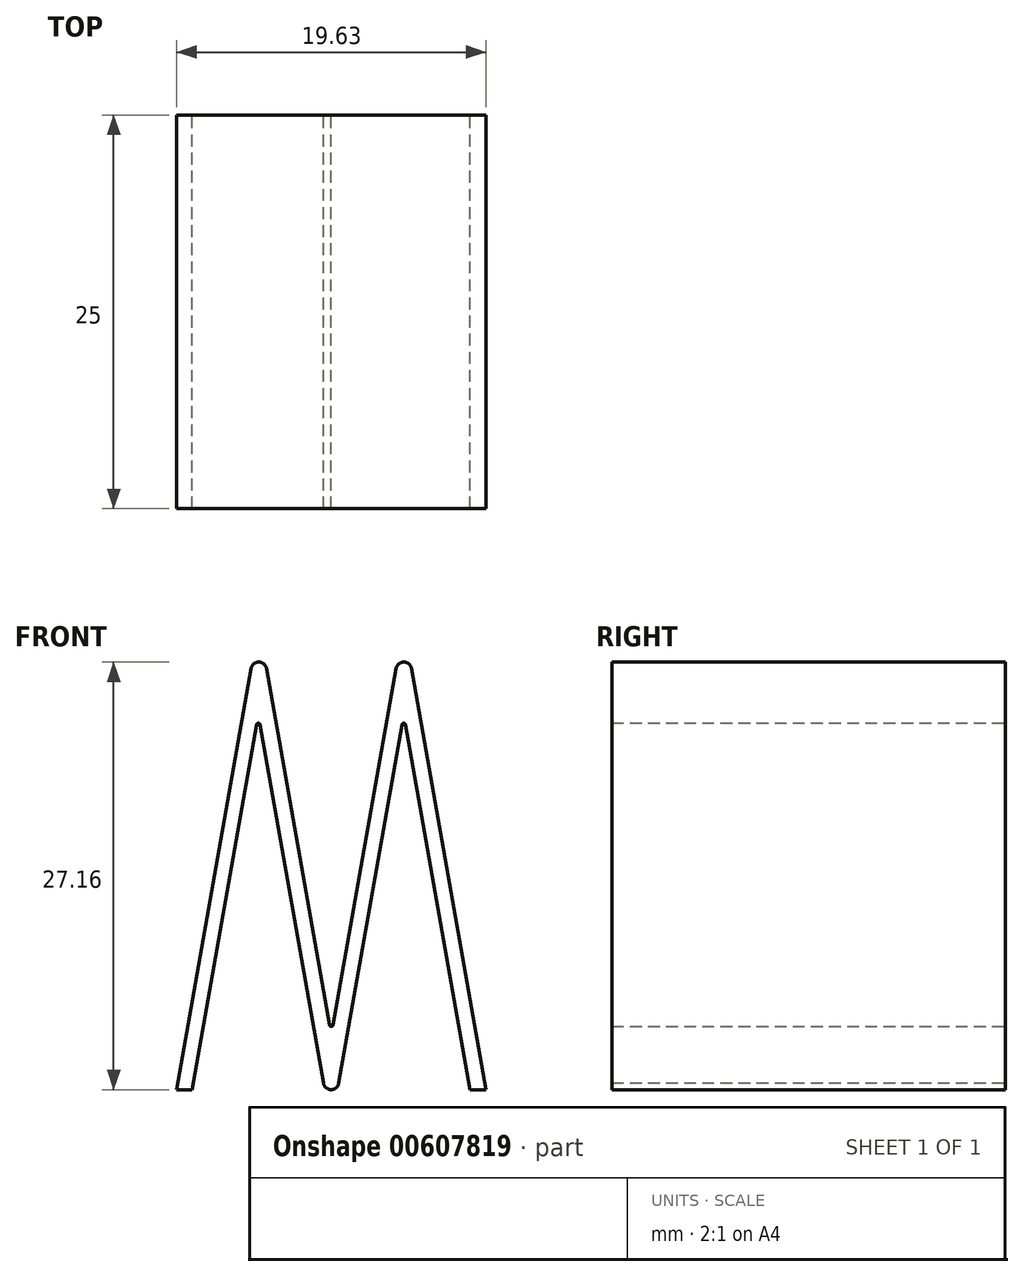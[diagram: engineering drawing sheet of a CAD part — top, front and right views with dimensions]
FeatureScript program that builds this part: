
annotation { "Feature Type Name" : "Feature", "Feature Type Description" : "" }
export const myFeature = defineFeature(function(context is Context, id is Id, definition is map)
    precondition{}
    {
        {
            var Q0;
            Q0=qCreatedBy(makeId("Front.planeOp"),FACE);
            var sketch = newSketch(context, id + "F0", { "sketchPlane" : qUnion([Q0])});
            skLineSegment(sketch, "E0", {"start": v(-0.5, 26.75) * mm, "end": v(-4.48, 4.12) * mm});
            skLineSegment(sketch, "E1", {"start": v(-4.63, 0) * mm, "end": v(-4.61, 0) * mm});
            skLineSegment(sketch, "E2", {"start": v(-4.14, 0.41) * mm, "end": v(-0.12, 23.17) * mm});
            skLineSegment(sketch, "E3.MirrorCS", {"start": v(0.5, 26.75) * mm, "end": v(5.2, 0) * mm});
            skLineSegment(sketch, "E4.MirrorCS", {"start": v(4.2, 0) * mm, "end": v(0.12, 23.17) * mm});
            skLineSegment(sketch, "E5.MirrorCS", {"start": v(5.2, 0) * mm, "end": v(4.2, 0) * mm});
            skPoint(sketch, "E6.visualSharp", {"position": v(0, 23.87) * mm});
            skArc(sketch, "E6.filletArc", {"start": v(0.12, 23.17) * mm, "mid": v(0, 23.28) * mm, "end": v(-0.12, 23.17) * mm});
            skPoint(sketch, "E7.visualSharp", {"position": v(0, 29.54) * mm});
            skArc(sketch, "E7.filletArc", {"start": v(0.5, 26.75) * mm, "mid": v(0, 27.16) * mm, "end": v(-0.5, 26.75) * mm});
            skPoint(sketch, "E8.visualSharp", {"position": v(-5.2, 0) * mm});
            skArc(sketch, "E8.filletArc", {"start": v(-5.1, 0.43) * mm, "mid": v(-4.94, 0.12) * mm, "end": v(-4.61, 0) * mm});
            skPoint(sketch, "E9.visualSharp", {"position": v(-4.2, 0) * mm});
            skArc(sketch, "E9.filletArc", {"start": v(-4.63, 0) * mm, "mid": v(-4.3, 0.12) * mm, "end": v(-4.14, 0.41) * mm});
            skLineSegment(sketch, "E10", {"start": v(-5.1, 0.59) * mm, "end": v(-4.1, 0.59) * mm, "construction": true});
            skLineSegment(sketch, "E11", {"start": v(-4.14, 0.41) * mm, "end": v(-5.1, 0.41) * mm, "construction": true});
            skCircle(sketch, "E12", {"center": v(-5.1, 0.41) * mm, "radius": 1.01 * mm, "construction": true});
            skCircle(sketch, "E13", {"center": v(-4.1, 0.59) * mm, "radius": 1.01 * mm, "construction": true});
            skLineSegment(sketch, "E14", {"start": v(-5.1, 0.41) * mm, "end": v(-4.1, 0.59) * mm, "construction": true});
            skLineSegment(sketch, "E15", {"start": v(-4.46, -0.37) * mm, "end": v(-4.76, 1.37) * mm, "construction": true});
            skLineSegment(sketch, "E16", {"start": v(-4.62, 0.59) * mm, "end": v(-4.62, 0.9) * mm, "construction": true});
            skLineSegment(sketch, "E17.MirrorCS", {"start": v(-5.1, 0.41) * mm, "end": v(-9.12, 23.17) * mm});
            skLineSegment(sketch, "E18.MirrorCS", {"start": v(-13.45, 0) * mm, "end": v(-9.37, 23.17) * mm});
            skArc(sketch, "E19.MirrorCS", {"start": v(-9.37, 23.17) * mm, "mid": v(-9.24, 23.28) * mm, "end": v(-9.12, 23.17) * mm});
            skLineSegment(sketch, "E20.MirrorCS", {"start": v(-14.42, 0) * mm, "end": v(-13.45, 0) * mm});
            skLineSegment(sketch, "E21", {"start": v(-4.6, 0.5) * mm, "end": v(-4.6, 0.64) * mm, "construction": true});
            skLineSegment(sketch, "E22.MirrorCS", {"start": v(-8.72, 26.75) * mm, "end": v(-4.73, 4.12) * mm});
            skLineSegment(sketch, "E23.MirrorCS", {"start": v(-9.7, 26.75) * mm, "end": v(-14.42, 0) * mm});
            skArc(sketch, "E24.MirrorCS", {"start": v(-9.7, 26.75) * mm, "mid": v(-9.21, 27.16) * mm, "end": v(-8.72, 26.75) * mm});
            skLineSegment(sketch, "E25.trimOffspring", {"start": v(-4.1, 0.59) * mm, "end": v(-4.1, 0.59) * mm});
            skPoint(sketch, "E26.visualSharp", {"position": v(-4.6, 3.42) * mm});
            skArc(sketch, "E26.filletArc", {"start": v(-4.73, 4.12) * mm, "mid": v(-4.6, 4.02) * mm, "end": v(-4.48, 4.12) * mm});
            skPoint(sketch, "E27.orphan", {"position": v(-14.45, 0) * mm});
            skSolve(sketch);
        }
        {
            var Q0;
            Q0=makeQuery(id+"F0.imprint","IMPRINT",FACE,{"disambiguationData":[TD([[makeQuery(id+"F0.imprint","IMPRINT",EDGE,{"derivedFrom":sQuery(id+"F0.wireOp",EDGE,"E0")}),1.0]])]});
            extrude(context, id + "F1", {"entities" : qUnion([Q0]), "depth" : 25 * mm, "offsetDistance" : 25 * mm});
        }
    });
